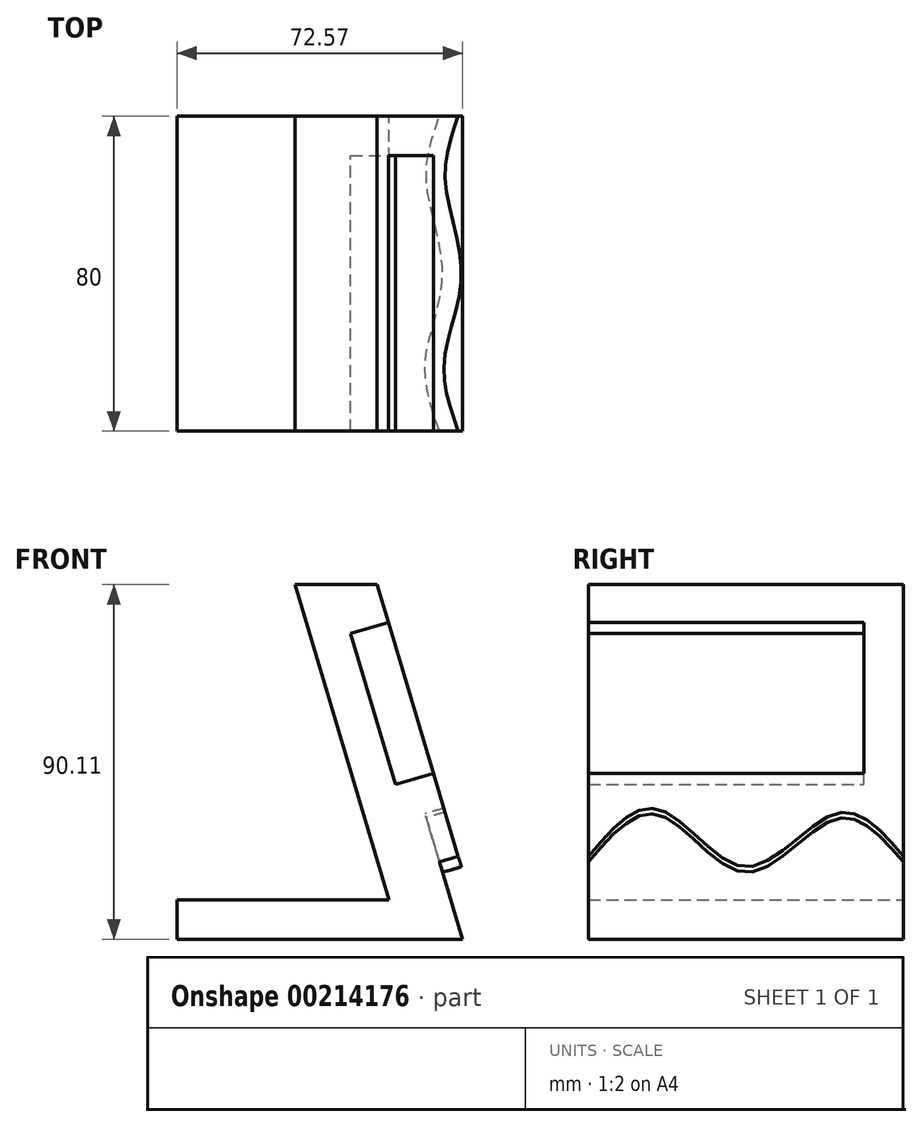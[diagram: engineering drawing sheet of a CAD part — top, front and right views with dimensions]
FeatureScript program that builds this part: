
annotation { "Feature Type Name" : "Feature", "Feature Type Description" : "" }
export const myFeature = defineFeature(function(context is Context, id is Id, definition is map)
    precondition{}
    {
        {
            var Q0;
            Q0=qCreatedBy(makeId("Front.planeOp"),FACE);
            var sketch = newSketch(context, id + "F0", { "sketchPlane" : qUnion([Q0])});
            skLineSegment(sketch, "E0", {"start": v(-21.54, -51.21) * mm, "end": v(56.24, -51.21) * mm});
            skLineSegment(sketch, "E1", {"start": v(-21.54, -41.21) * mm, "end": v(-21.54, -51.21) * mm});
            skLineSegment(sketch, "E2", {"start": v(56.24, -51.21) * mm, "end": v(29.37, 38.9) * mm});
            skLineSegment(sketch, "E3.0", {"start": v(35.37, -51.21) * mm, "end": v(8.5, 38.9) * mm});
            skLineSegment(sketch, "E4", {"start": v(-21.54, -41.21) * mm, "end": v(32.4, -41.21) * mm});
            skLineSegment(sketch, "E5", {"start": v(8.5, 38.9) * mm, "end": v(29.37, 38.9) * mm});
            skSolve(sketch);
        }
        {
            var Q0;
            Q0=makeQuery(id+"F0.imprint","IMPRINT",FACE,{"disambiguationData":[TD([[makeQuery(id+"F0.imprint","IMPRINT",EDGE,{"derivedFrom":sQuery(id+"F0.wireOp",EDGE,"E0")}),1.0]])]});
            var Q1;
            {var subQ5=sQuery(id+"F0.wireOp",EDGE,"E2");Q1=makeQuery(id+"F0.imprint","IMPRINT",FACE,{"disambiguationData":[TD([[makeQuery(id+"F0.imprint","IMPRINT",EDGE,{"derivedFrom":subQ5}),1.0]])]});}
            extrude(context, id + "F1", {"entities" : qUnion([Q0, Q1]), "endBound" : BoundingType.SYMMETRIC, "depth" : 80 * mm});
        }
        {
            var Q0;
            Q0=makeQuery(id+"F1.opExtrude","SWEPT_FACE",FACE,{"disambiguationData":[OSD([sQuery(id+"F0.wireOp",EDGE,"E2")])]});
            var sketch = newSketch(context, id + "F2", { "sketchPlane" : qUnion([Q0])});
            skLineSegment(sketch, "E6.bottom", {"start": v(-40, 18.88) * mm, "end": v(30, 18.88) * mm});
            skLineSegment(sketch, "E6.top", {"start": v(-40, -21.12) * mm, "end": v(30, -21.12) * mm});
            skLineSegment(sketch, "E6.left", {"start": v(-40, 18.88) * mm, "end": v(-40, -21.12) * mm});
            skLineSegment(sketch, "E6.right", {"start": v(30, 18.88) * mm, "end": v(30, -21.12) * mm});
            skSolve(sketch);
        }
        {
            var Q0;
            Q0=makeQuery(id+"F2.imprint","IMPRINT",FACE,{"disambiguationData":[TD([[makeQuery(id+"F2.imprint","IMPRINT",EDGE,{"derivedFrom":sQuery(id+"F2.wireOp",EDGE,"E6.bottom")}),-1.0]])]});
            extrude(context, id + "F3", {"entities" : qUnion([Q0]), "operationType" : NewBodyOperationType.REMOVE, "oppositeDirection" : true, "depth" : 10 * mm});
        }
        {
            var Q0;
            Q0=makeQuery(id+"F1.opExtrude","SWEPT_FACE",FACE,{"disambiguationData":[OSD([sQuery(id+"F0.wireOp",EDGE,"E2")])]});
            var sketch = newSketch(context, id + "F4", { "sketchPlane" : qUnion([Q0])});
            skPoint(sketch, "E7.4.internal.snap0", {"position": v(-40, -43.14) * mm});
            skFitSpline(sketch, "E7", {"points": [v(-40, -43.14) * mm, v(-22.19, -30.67) * mm, v(0, -45.91) * mm, v(23.2, -31.7) * mm, v(40, -43.14) * mm], "startDerivative": vector(73, 89.7) * mm, "endDerivative": vector(69.38, -84.8) * mm});
            skFitSpline(sketch, "E8.0", {"points": [v(-36.12, -46.3) * mm, v(-35.36, -45.36) * mm, v(-33.86, -43.52) * mm, v(-31.69, -40.97) * mm, v(-29.6, -38.76) * mm, v(-27.67, -37.03) * mm, v(-26.27, -36.1) * mm, v(-25.37, -35.66) * mm, v(-24.8, -35.48) * mm, v(-24.37, -35.4) * mm, v(-24.08, -35.4) * mm, v(-23.85, -35.42) * mm, v(-23.66, -35.45) * mm, v(-23.47, -35.5) * mm, v(-23.2, -35.6) * mm, v(-22.88, -35.75) * mm, v(-22.38, -36.02) * mm, v(-21.65, -36.48) * mm, v(-20.65, -37.24) * mm, v(-19.18, -38.47) * mm, v(-17.16, -40.36) * mm, v(-14.54, -42.91) * mm, v(-12.18, -45.09) * mm, v(-10.15, -46.74) * mm, v(-8.55, -47.91) * mm, v(-6.82, -48.97) * mm, v(-4.96, -49.89) * mm, v(-3.25, -50.46) * mm, v(-1.78, -50.77) * mm, v(-0.64, -50.9) * mm, v(0.54, -50.93) * mm, v(1.68, -50.85) * mm, v(2.78, -50.68) * mm, v(4.2, -50.33) * mm, v(5.85, -49.74) * mm, v(7.69, -48.84) * mm, v(9.4, -47.8) * mm, v(11.57, -46.3) * mm, v(14.1, -44.28) * mm, v(16.93, -41.82) * mm, v(19.1, -39.94) * mm, v(20.72, -38.67) * mm, v(21.84, -37.86) * mm, v(22.84, -37.22) * mm, v(23.7, -36.78) * mm, v(24.24, -36.58) * mm, v(24.55, -36.5) * mm, v(24.76, -36.47) * mm, v(24.96, -36.45) * mm, v(25.22, -36.45) * mm, v(25.57, -36.49) * mm, v(26.08, -36.62) * mm, v(26.9, -36.96) * mm, v(28.17, -37.75) * mm, v(29.98, -39.28) * mm, v(31.93, -41.3) * mm, v(33.99, -43.68) * mm, v(35.4, -45.42) * mm, v(36.13, -46.3) * mm]});
            skLineSegment(sketch, "E9", {"start": v(-35.66, -45.73) * mm, "end": v(-40, -48.62) * mm});
            skLineSegment(sketch, "E10", {"start": v(36.13, -46.3) * mm, "end": v(40, -49.98) * mm});
            skLineSegment(sketch, "E11", {"start": v(-40, -48.62) * mm, "end": v(-40, -43.14) * mm});
            skLineSegment(sketch, "E12", {"start": v(40, -49.98) * mm, "end": v(40, -43.14) * mm});
            skSolve(sketch);
        }
        {
            var Q0;
            Q0=makeQuery(id+"F4.imprint","IMPRINT",FACE,{"disambiguationData":[TD([[makeQuery(id+"F4.imprint","IMPRINT",EDGE,{"derivedFrom":sQuery(id+"F4.wireOp",EDGE,"E7")}),-1.0]])]});
            extrude(context, id + "F5", {"entities" : qUnion([Q0]), "operationType" : NewBodyOperationType.REMOVE, "oppositeDirection" : true, "depth" : 5 * mm});
        }
    });
